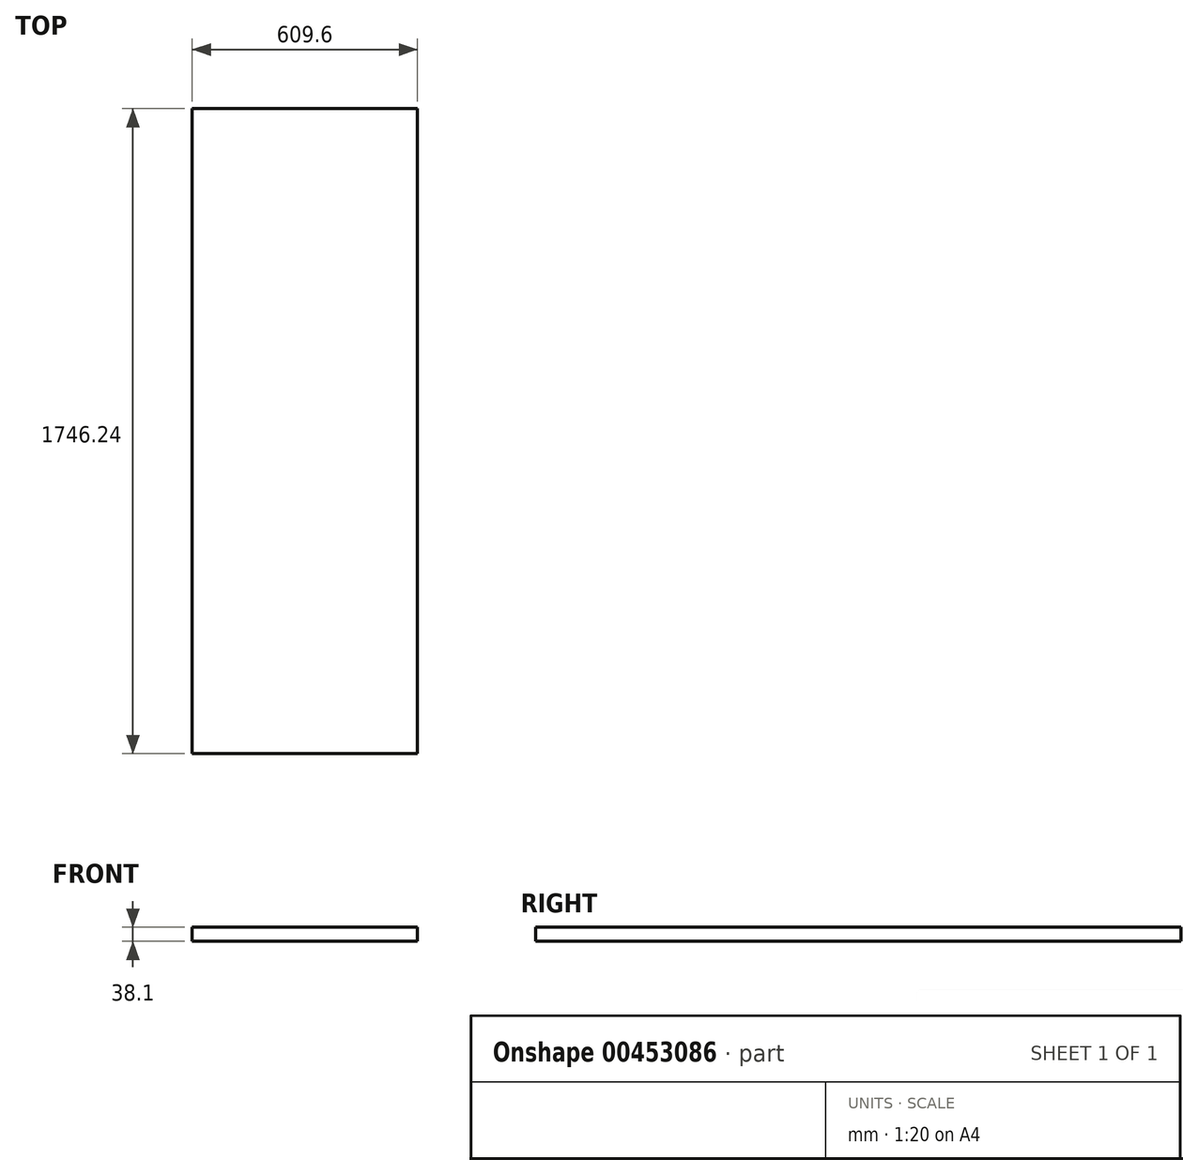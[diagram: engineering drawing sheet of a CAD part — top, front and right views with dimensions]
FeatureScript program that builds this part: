
annotation { "Feature Type Name" : "Feature", "Feature Type Description" : "" }
export const myFeature = defineFeature(function(context is Context, id is Id, definition is map)
    precondition{}
    {
        {
            var Q0;
            Q0=qCreatedBy(makeId("Top.planeOp"),FACE);
            var sketch = newSketch(context, id + "F0", { "sketchPlane" : qUnion([Q0])});
            skLineSegment(sketch, "E0.bottom", {"start": v(304.8, 873.12) * mm, "end": v(-304.8, 873.12) * mm});
            skLineSegment(sketch, "E0.top", {"start": v(304.8, -873.13) * mm, "end": v(-304.8, -873.13) * mm});
            skLineSegment(sketch, "E0.left", {"start": v(304.8, 873.12) * mm, "end": v(304.8, -873.13) * mm});
            skLineSegment(sketch, "E0.right", {"start": v(-304.8, 873.12) * mm, "end": v(-304.8, -873.13) * mm});
            skPoint(sketch, "E0.middle", {"position": v(0, 0) * mm});
            skSolve(sketch);
        }
        {
            var Q0;
            Q0 = qSketchRegion(id + "F0", true);
            extrude(context, id + "F1", {"entities" : qUnion([Q0]), "depth" : 38.1 * mm, "offsetDistance" : 25.4 * mm});
        }
    });
